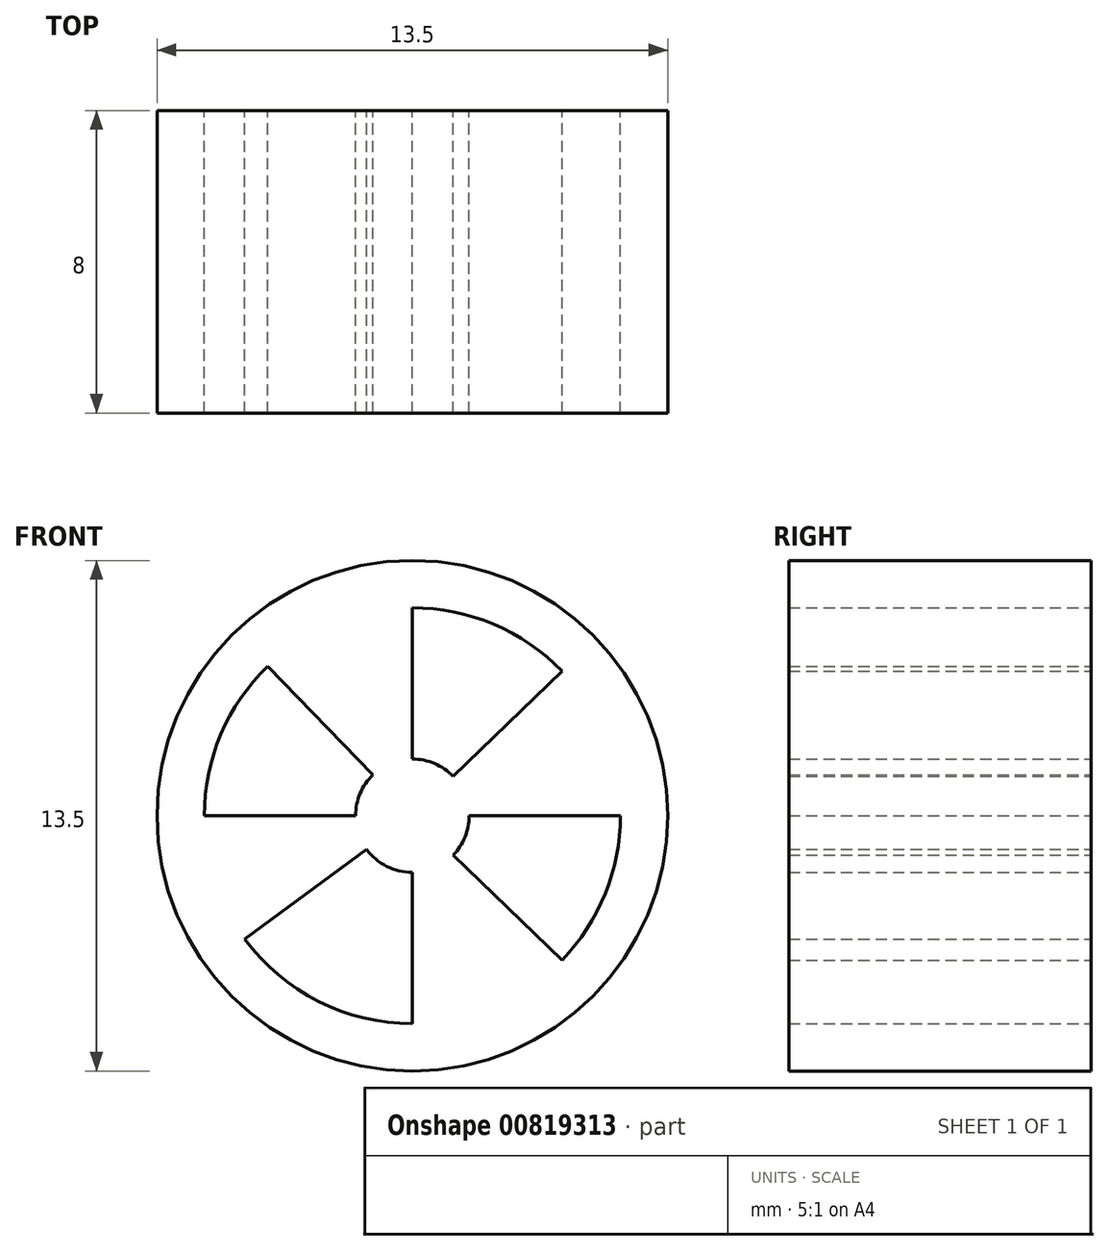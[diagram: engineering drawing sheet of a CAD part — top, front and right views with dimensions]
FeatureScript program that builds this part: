
annotation { "Feature Type Name" : "Feature", "Feature Type Description" : "" }
export const myFeature = defineFeature(function(context is Context, id is Id, definition is map)
    precondition{}
    {
        {
            var Q0;
            Q0=qCreatedBy(makeId("Front.planeOp"),FACE);
            var sketch = newSketch(context, id + "F0", { "sketchPlane" : qUnion([Q0])});
            skCircle(sketch, "E0", {"center": v(0, 0) * mm, "radius": 6.75 * mm});
            skSolve(sketch);
        }
        {
            var Q0;
            Q0=makeQuery(id+"F0.imprint","IMPRINT",FACE,{"disambiguationData":[TD([[makeQuery(id+"F0.imprint","IMPRINT",EDGE,{"derivedFrom":sQuery(id+"F0.wireOp",EDGE,"E0")}),1.0]])]});
            extrude(context, id + "F1", {"entities" : qUnion([Q0]), "depth" : 8 * mm, "offsetDistance" : 25 * mm});
        }
        {
            var Q0;
            Q0=makeQuery(id+"F1.opExtrude","CAP_FACE",FACE,{"disambiguationData":[OSD([sQuery(id+"F0.wireOp",EDGE,"E0")])],"isStart":true});
            var sketch = newSketch(context, id + "F2", { "sketchPlane" : qUnion([Q0])});
            skCircle(sketch, "E1", {"center": v(0, 0) * mm, "radius": 5.5 * mm});
            skCircle(sketch, "E2", {"center": v(0, 0) * mm, "radius": 1.5 * mm});
            skLineSegment(sketch, "E3", {"start": v(0, 0) * mm, "end": v(0, 5.5) * mm});
            skLineSegment(sketch, "E4", {"start": v(0, 0) * mm, "end": v(0, -5.5) * mm});
            skLineSegment(sketch, "E5", {"start": v(0, 0) * mm, "end": v(5.5, 0) * mm});
            skLineSegment(sketch, "E6", {"start": v(0, 0) * mm, "end": v(-5.5, 0) * mm});
            skLineSegment(sketch, "E7", {"start": v(0, 0) * mm, "end": v(-3.96, 3.82) * mm});
            skLineSegment(sketch, "E8", {"start": v(0, 0) * mm, "end": v(3.82, 3.96) * mm});
            skLineSegment(sketch, "E9", {"start": v(0, 0) * mm, "end": v(4.43, -3.26) * mm});
            skLineSegment(sketch, "E10", {"start": v(0, 0) * mm, "end": v(-3.96, -3.82) * mm});
            skSolve(sketch);
        }
        {
            var Q0;
            {var subQ0=sQuery(id+"F2.wireOp",EDGE,"E3");var subQ1=sQuery(id+"F2.wireOp",EDGE,"E1");var subQ2=makeQuery(id+"F2.imprint","INTERSECT",VERTEX,{"derivedFrom":[subQ1,subQ0]});Q0=makeQuery(id+"F2.imprint","IMPRINT",FACE,{"disambiguationData":[TD([[makeQuery(id+"F2.imprint","IMPRINT",EDGE,{"disambiguationData":[TD([[subQ2,-1.0]])],"derivedFrom":subQ1}),1.0]])]});}
            extrude(context, id + "F3", {"entities" : qUnion([Q0]), "operationType" : NewBodyOperationType.REMOVE, "endBound" : BoundingType.THROUGH_ALL, "oppositeDirection" : true, "depth" : 25 * mm, "offsetDistance" : 25 * mm});
        }
        {
            var Q0;
            {var subQ0=sQuery(id+"F2.wireOp",EDGE,"E5");var subQ1=sQuery(id+"F2.wireOp",EDGE,"E1");var subQ2=makeQuery(id+"F2.imprint","INTERSECT",VERTEX,{"derivedFrom":[subQ1,subQ0]});Q0=makeQuery(id+"F2.imprint","IMPRINT",FACE,{"disambiguationData":[TD([[makeQuery(id+"F2.imprint","IMPRINT",EDGE,{"disambiguationData":[TD([[subQ2,-1.0]])],"derivedFrom":subQ1}),1.0]])]});}
            var Q1;
            {var subQ0=sQuery(id+"F2.wireOp",EDGE,"E4");var subQ1=sQuery(id+"F2.wireOp",EDGE,"E1");var subQ2=makeQuery(id+"F2.imprint","INTERSECT",VERTEX,{"derivedFrom":[subQ1,subQ0]});Q1=makeQuery(id+"F2.imprint","IMPRINT",FACE,{"disambiguationData":[TD([[makeQuery(id+"F2.imprint","IMPRINT",EDGE,{"disambiguationData":[TD([[subQ2,-1.0]])],"derivedFrom":subQ1}),1.0]])]});}
            var Q2;
            {var subQ0=sQuery(id+"F2.wireOp",EDGE,"E6");var subQ1=sQuery(id+"F2.wireOp",EDGE,"E1");var subQ2=makeQuery(id+"F2.imprint","INTERSECT",VERTEX,{"derivedFrom":[subQ1,subQ0]});Q2=makeQuery(id+"F2.imprint","IMPRINT",FACE,{"disambiguationData":[TD([[makeQuery(id+"F2.imprint","IMPRINT",EDGE,{"disambiguationData":[TD([[subQ2,-1.0]])],"derivedFrom":subQ1}),1.0]])]});}
            var Q3;
            {var subQ0=sQuery(id+"F2.wireOp",EDGE,"E3");var subQ1=sQuery(id+"F2.wireOp",EDGE,"E1");var subQ2=makeQuery(id+"F2.imprint","INTERSECT",VERTEX,{"derivedFrom":[subQ1,subQ0]});Q3=makeQuery(id+"F2.imprint","IMPRINT",FACE,{"disambiguationData":[TD([[makeQuery(id+"F2.imprint","IMPRINT",EDGE,{"disambiguationData":[TD([[subQ2,-1.0]])],"derivedFrom":subQ1}),1.0]])]});}
            extrude(context, id + "F4", {"entities" : qUnion([Q0, Q1, Q2, Q3]), "operationType" : NewBodyOperationType.REMOVE, "endBound" : BoundingType.THROUGH_ALL, "oppositeDirection" : true, "depth" : 25 * mm, "offsetDistance" : 25 * mm});
        }
    });
